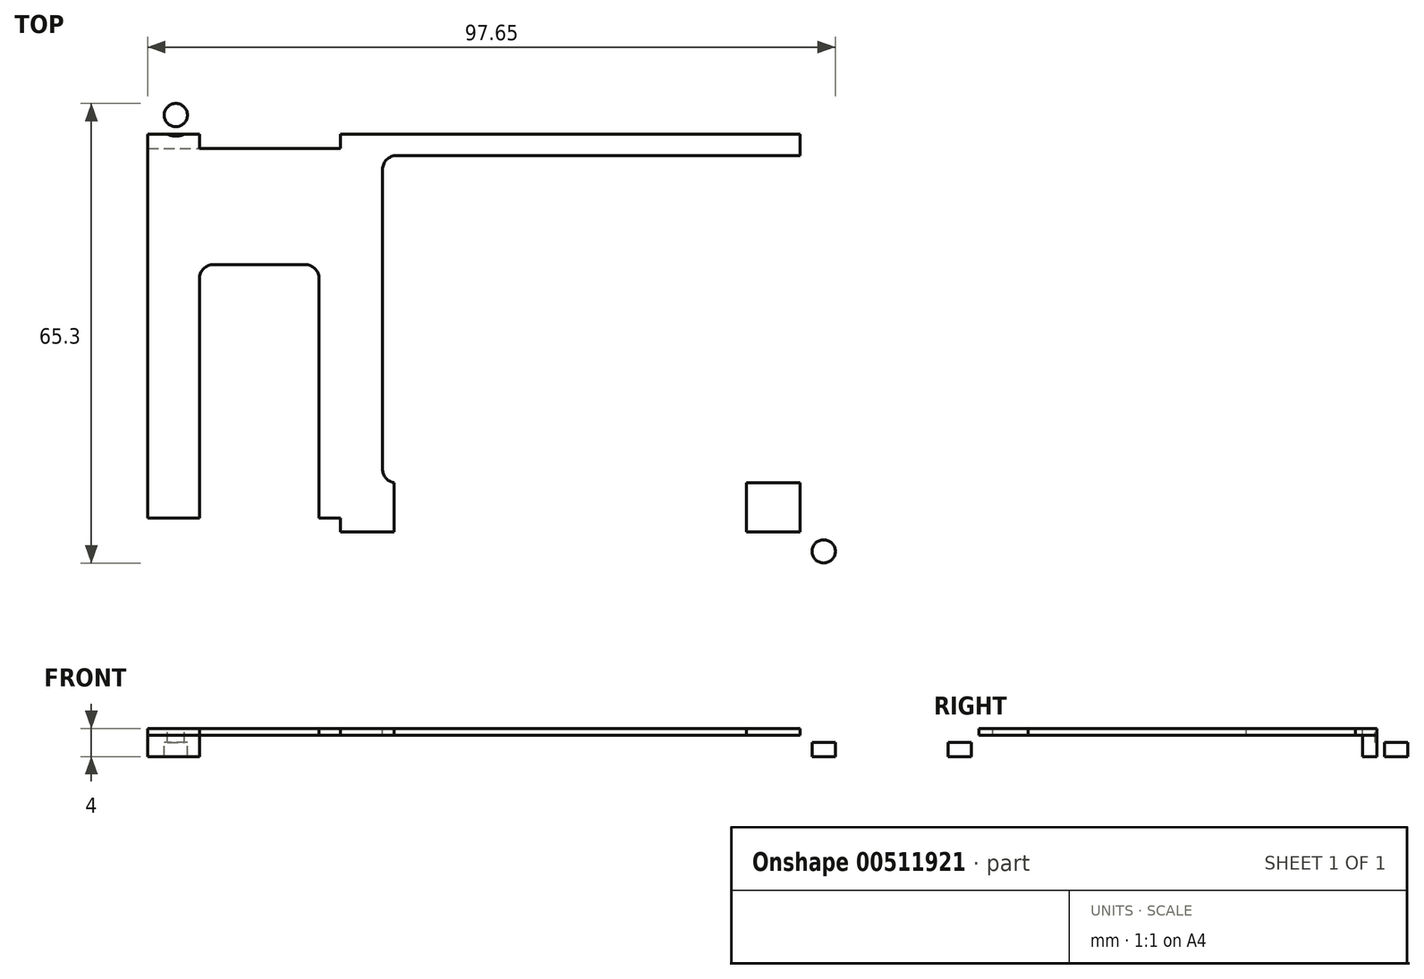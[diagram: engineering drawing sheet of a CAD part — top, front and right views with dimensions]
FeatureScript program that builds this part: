
annotation { "Feature Type Name" : "Feature", "Feature Type Description" : "" }
export const myFeature = defineFeature(function(context is Context, id is Id, definition is map)
    precondition{}
    {
        {
            var Q0;
            Q0=qCreatedBy(makeId("Top.planeOp"),FACE);
            var sketch = newSketch(context, id + "F0", { "sketchPlane" : qUnion([Q0])});
            skLineSegment(sketch, "E0.bottom", {"start": v(-50, 35) * mm, "end": v(50, 35) * mm});
            skLineSegment(sketch, "E0.top", {"start": v(-50, -35) * mm, "end": v(50, -35) * mm});
            skLineSegment(sketch, "E0.left", {"start": v(-50, 35) * mm, "end": v(-50, -35) * mm});
            skLineSegment(sketch, "E0.right", {"start": v(50, 35) * mm, "end": v(50, -35) * mm});
            skPoint(sketch, "E1", {"position": v(-50, 0) * mm});
            skPoint(sketch, "E2", {"position": v(0, 35) * mm});
            skSolve(sketch);
        }
        {
            var Q0;
            Q0=makeQuery(id+"F0.imprint","IMPRINT",FACE,{"disambiguationData":[TD([[makeQuery(id+"F0.imprint","IMPRINT",EDGE,{"derivedFrom":sQuery(id+"F0.wireOp",EDGE,"E0.bottom")}),-1.0]])]});
            extrude(context, id + "F1", {"entities" : qUnion([Q0]), "depth" : 4 * mm});
        }
        {
            var Q0;
            Q0=makeQuery(id+"F1.opExtrude","CAP_FACE",FACE,{"disambiguationData":[OSD([sQuery(id+"F0.wireOp",EDGE,"E0.bottom"),sQuery(id+"F0.wireOp",EDGE,"E0.top"),sQuery(id+"F0.wireOp",EDGE,"E0.left"),sQuery(id+"F0.wireOp",EDGE,"E0.right")])],"isStart":false});
            var sketch = newSketch(context, id + "F2", { "sketchPlane" : qUnion([Q0])});
            skLineSegment(sketch, "E3.bottom", {"start": v(-42.65, 28.25) * mm, "end": v(42.65, 28.25) * mm, "construction": true});
            skLineSegment(sketch, "E3.top", {"start": v(-42.65, -28.25) * mm, "end": v(42.65, -28.25) * mm, "construction": true});
            skLineSegment(sketch, "E3.left", {"start": v(-42.65, 28.25) * mm, "end": v(-42.65, -28.25) * mm});
            skLineSegment(sketch, "E3.right", {"start": v(42.65, 28.25) * mm, "end": v(42.65, -28.25) * mm, "construction": true});
            skPoint(sketch, "E4", {"position": v(0, 28.25) * mm});
            skPoint(sketch, "E5", {"position": v(42.65, 0) * mm});
            skCircle(sketch, "E6", {"center": v(46, 31) * mm, "radius": 1.65 * mm});
            skCircle(sketch, "E7.MirrorC", {"center": v(-46, 31) * mm, "radius": 1.65 * mm});
            skCircle(sketch, "E8.MirrorC", {"center": v(46, -31) * mm, "radius": 1.65 * mm});
            skCircle(sketch, "E9.MirrorC", {"center": v(-46, -31) * mm, "radius": 1.65 * mm});
            skLineSegment(sketch, "E10.bottom", {"start": v(-42.65, 28.25) * mm, "end": v(-50, 28.25) * mm});
            skLineSegment(sketch, "E10.top", {"start": v(-42.65, -26.25) * mm, "end": v(-50, -26.25) * mm});
            skLineSegment(sketch, "E10.left", {"start": v(-42.65, 28.25) * mm, "end": v(-42.65, -26.25) * mm, "construction": true});
            skLineSegment(sketch, "E10.right", {"start": v(-50, 28.25) * mm, "end": v(-50, -26.25) * mm});
            skLineSegment(sketch, "E11.bottom", {"start": v(42.65, 6.25) * mm, "end": v(46.15, 6.25) * mm, "construction": true});
            skLineSegment(sketch, "E11.top", {"start": v(42.65, -6.25) * mm, "end": v(46.15, -6.25) * mm, "construction": true});
            skLineSegment(sketch, "E11.left", {"start": v(42.65, 6.25) * mm, "end": v(42.65, -6.25) * mm});
            skLineSegment(sketch, "E11.right", {"start": v(46.15, 6.25) * mm, "end": v(46.15, -6.25) * mm, "construction": true});
            skLineSegment(sketch, "E12", {"start": v(-50, 26.25) * mm, "end": v(-22.65, 26.25) * mm});
            skLineSegment(sketch, "E13", {"start": v(-22.65, 26.25) * mm, "end": v(-22.65, 28.25) * mm});
            skLineSegment(sketch, "E14", {"start": v(-22.65, 28.25) * mm, "end": v(42.65, 28.25) * mm});
            skLineSegment(sketch, "E15", {"start": v(42.65, 25.25) * mm, "end": v(48, 25.25) * mm});
            skLineSegment(sketch, "E16", {"start": v(48, -21.25) * mm, "end": v(42.65, -21.25) * mm});
            skLineSegment(sketch, "E17", {"start": v(-22.65, -26.25) * mm, "end": v(-22.65, -28.25) * mm});
            skLineSegment(sketch, "E18", {"start": v(-22.65, -26.25) * mm, "end": v(-50, -26.25) * mm});
            skLineSegment(sketch, "E19", {"start": v(-50, -26.25) * mm, "end": v(-50, 26.25) * mm});
            skLineSegment(sketch, "E20", {"start": v(42.65, 28.25) * mm, "end": v(42.65, 25.25) * mm});
            skLineSegment(sketch, "E21", {"start": v(-22.65, -28.25) * mm, "end": v(-15, -28.25) * mm});
            skLineSegment(sketch, "E22", {"start": v(-15, -28.25) * mm, "end": v(-15, -21.25) * mm});
            skLineSegment(sketch, "E23", {"start": v(-15, -21.25) * mm, "end": v(35, -21.25) * mm});
            skLineSegment(sketch, "E24", {"start": v(35, -21.25) * mm, "end": v(35, -28.25) * mm});
            skLineSegment(sketch, "E25", {"start": v(35, -28.25) * mm, "end": v(42.65, -28.25) * mm});
            skLineSegment(sketch, "E26", {"start": v(42.65, -28.25) * mm, "end": v(42.65, -21.25) * mm});
            skLineSegment(sketch, "E27.bottom", {"start": v(48, 25.25) * mm, "end": v(-16.65, 25.25) * mm});
            skLineSegment(sketch, "E27.top", {"start": v(48, -21.25) * mm, "end": v(-16.65, -21.25) * mm});
            skLineSegment(sketch, "E27.left", {"start": v(48, 25.25) * mm, "end": v(48, -21.25) * mm});
            skLineSegment(sketch, "E27.right", {"start": v(-16.65, 25.25) * mm, "end": v(-16.65, -21.25) * mm});
            skLineSegment(sketch, "E28.bottom", {"start": v(-16.65, 25.25) * mm, "end": v(42.65, 25.25) * mm});
            skLineSegment(sketch, "E28.top", {"start": v(-16.65, 28.25) * mm, "end": v(42.65, 28.25) * mm});
            skLineSegment(sketch, "E28.left", {"start": v(-16.65, 25.25) * mm, "end": v(-16.65, 28.25) * mm});
            skLineSegment(sketch, "E28.right", {"start": v(42.65, 25.25) * mm, "end": v(42.65, 28.25) * mm});
            skLineSegment(sketch, "E29", {"start": v(48, -21.25) * mm, "end": v(48, -21.25) * mm});
            skLineSegment(sketch, "E30.bottom", {"start": v(-42.65, 9.75) * mm, "end": v(-25.65, 9.75) * mm});
            skLineSegment(sketch, "E30.top", {"start": v(-42.65, -26.25) * mm, "end": v(-25.65, -26.25) * mm});
            skLineSegment(sketch, "E30.left", {"start": v(-42.65, 9.75) * mm, "end": v(-42.65, -26.25) * mm});
            skLineSegment(sketch, "E30.right", {"start": v(-25.65, 9.75) * mm, "end": v(-25.65, -26.25) * mm});
            skSolve(sketch);
        }
        {
            var Q0;
            Q0=makeQuery(id+"F2.imprint","IMPRINT",FACE,{"disambiguationData":[TD([[makeQuery(id+"F2.imprint","IMPRINT",EDGE,{"derivedFrom":sQuery(id+"F2.wireOp",EDGE,"E7.MirrorC")}),-1.0]])]});
            var Q1;
            Q1=makeQuery(id+"F2.imprint","IMPRINT",FACE,{"disambiguationData":[TD([[makeQuery(id+"F2.imprint","IMPRINT",EDGE,{"derivedFrom":sQuery(id+"F2.wireOp",EDGE,"E6")}),1.0]])]});
            var Q2;
            Q2=makeQuery(id+"F2.imprint","IMPRINT",FACE,{"disambiguationData":[TD([[makeQuery(id+"F2.imprint","IMPRINT",EDGE,{"derivedFrom":sQuery(id+"F2.wireOp",EDGE,"E8.MirrorC")}),-1.0]])]});
            var Q3;
            Q3=makeQuery(id+"F2.imprint","IMPRINT",FACE,{"disambiguationData":[TD([[makeQuery(id+"F2.imprint","IMPRINT",EDGE,{"derivedFrom":sQuery(id+"F2.wireOp",EDGE,"E9.MirrorC")}),1.0]])]});
            extrude(context, id + "F3", {"entities" : qUnion([Q0, Q1, Q2, Q3]), "operationType" : NewBodyOperationType.REMOVE, "endBound" : BoundingType.UP_TO_NEXT, "oppositeDirection" : true, "depth" : 25 * mm});
        }
        {
            var Q0;
            Q0=makeQuery(id+"F2.imprint","IMPRINT",FACE,{"disambiguationData":[TD([[makeQuery(id+"F2.imprint","IMPRINT",EDGE,{"derivedFrom":sQuery(id+"F2.wireOp",EDGE,"E27.bottom")}),1.0]])]});
            var Q1;
            Q1=makeQuery(id+"F2.imprint","IMPRINT",FACE,{"disambiguationData":[TD([[makeQuery(id+"F2.imprint","IMPRINT",EDGE,{"derivedFrom":sQuery(id+"F2.wireOp",EDGE,"E28.bottom")}),1.0]])]});
            var Q2;
            {var subQ5=sQuery(id+"F2.wireOp",EDGE,"E19");Q2=makeQuery(id+"F2.imprint","IMPRINT",FACE,{"disambiguationData":[TD([[makeQuery(id+"F2.imprint","IMPRINT",EDGE,{"derivedFrom":subQ5}),1.0]])]});}
            var Q3;
            Q3=makeQuery(id+"F2.imprint","IMPRINT",FACE,{"disambiguationData":[TD([[makeQuery(id+"F2.imprint","IMPRINT",EDGE,{"derivedFrom":sQuery(id+"F2.wireOp",EDGE,"E30.bottom")}),-1.0]])]});
            extrude(context, id + "F4", {"entities" : qUnion([Q0, Q1, Q2, Q3]), "operationType" : NewBodyOperationType.REMOVE, "endBound" : BoundingType.UP_TO_NEXT, "oppositeDirection" : true, "depth" : 25 * mm});
        }
        {
            var Q0;
            Q0=makeQuery(id+"F0.imprint","IMPRINT",FACE,{"disambiguationData":[TD([[makeQuery(id+"F0.imprint","IMPRINT",EDGE,{"derivedFrom":sQuery(id+"F0.wireOp",EDGE,"E0.bottom")}),-1.0]])]});
            var sketch = newSketch(context, id + "F5", { "sketchPlane" : qUnion([Q0])});
            skLineSegment(sketch, "E31.0", {"start": v(-22.65, -26.25) * mm, "end": v(-50, -26.25) * mm});
            skLineSegment(sketch, "E32.0", {"start": v(-50, 26.25) * mm, "end": v(-22.65, 26.25) * mm});
            skPoint(sketch, "E33.0", {"position": v(-22.65, 27.25) * mm});
            skLineSegment(sketch, "E34.0", {"start": v(-22.65, 26.25) * mm, "end": v(-22.65, 28.25) * mm});
            skLineSegment(sketch, "E35.0", {"start": v(-22.65, 28.25) * mm, "end": v(42.65, 28.25) * mm});
            skLineSegment(sketch, "E36.0", {"start": v(-22.65, -26.25) * mm, "end": v(-22.65, -28.25) * mm});
            skLineSegment(sketch, "E37.0", {"start": v(-22.65, -28.25) * mm, "end": v(-15, -28.25) * mm});
            skLineSegment(sketch, "E38.0", {"start": v(-15, -28.25) * mm, "end": v(-15, -21.25) * mm});
            skLineSegment(sketch, "E39.0", {"start": v(35, -21.25) * mm, "end": v(35, -28.25) * mm});
            skLineSegment(sketch, "E40.0", {"start": v(42.65, -28.25) * mm, "end": v(42.65, -21.25) * mm});
            skLineSegment(sketch, "E41.0", {"start": v(48, -21.25) * mm, "end": v(42.65, -21.25) * mm});
            skLineSegment(sketch, "E42", {"start": v(35, -28.25) * mm, "end": v(42.65, -28.25) * mm});
            skLineSegment(sketch, "E43", {"start": v(-50, -26.25) * mm, "end": v(-50, 26.25) * mm});
            skLineSegment(sketch, "E44.0", {"start": v(42.65, 28.25) * mm, "end": v(42.65, 25.25) * mm});
            skLineSegment(sketch, "E45.0", {"start": v(42.65, 25.25) * mm, "end": v(48, 25.25) * mm});
            skLineSegment(sketch, "E46", {"start": v(48, -21.25) * mm, "end": v(48, 25.25) * mm});
            skLineSegment(sketch, "E47", {"start": v(-15, -21.25) * mm, "end": v(35, -21.25) * mm});
            skSolve(sketch);
        }
        {
            var Q0;
            Q0=makeQuery(id+"F5.imprint","IMPRINT",FACE,{"disambiguationData":[TD([[makeQuery(id+"F5.imprint","IMPRINT",EDGE,{"derivedFrom":sQuery(id+"F5.wireOp",EDGE,"E31.0")}),-1.0]])]});
            extrude(context, id + "F6", {"entities" : qUnion([Q0]), "operationType" : NewBodyOperationType.REMOVE, "depth" : 3 * mm});
        }
        {
            var Q0;
            Q0=makeQuery(id+"F1.opExtrude","CAP_FACE",FACE,{"disambiguationData":[OSD([sQuery(id+"F0.wireOp",EDGE,"E0.bottom"),sQuery(id+"F0.wireOp",EDGE,"E0.top"),sQuery(id+"F0.wireOp",EDGE,"E0.left"),sQuery(id+"F0.wireOp",EDGE,"E0.right")])],"isStart":false});
            var sketch = newSketch(context, id + "F7", { "sketchPlane" : qUnion([Q0])});
            skCircle(sketch, "E48", {"center": v(-46, 31) * mm, "radius": 3 * mm});
            skCircle(sketch, "E49", {"center": v(46, 31) * mm, "radius": 3 * mm});
            skCircle(sketch, "E50", {"center": v(46, -31) * mm, "radius": 3 * mm});
            skCircle(sketch, "E51", {"center": v(-46, -31) * mm, "radius": 3 * mm});
            skSolve(sketch);
        }
        {
            var Q0;
            Q0 = qSketchRegion(id + "F7", true);
            extrude(context, id + "F8", {"entities" : qUnion([Q0]), "operationType" : NewBodyOperationType.REMOVE, "oppositeDirection" : true, "depth" : 2 * mm});
        }
        {
            var Q0;
            Q0=makeQuery(id+"F1.opExtrude","SWEPT_EDGE",EDGE,{"disambiguationData":[OSD([sQuery(id+"F0.wireOp",EDGE,"E0.bottom"),sQuery(id+"F0.wireOp",EDGE,"E0.left")])]});
            var Q1;
            Q1=makeQuery(id+"F1.opExtrude","SWEPT_EDGE",EDGE,{"disambiguationData":[OSD([sQuery(id+"F0.wireOp",EDGE,"E0.top"),sQuery(id+"F0.wireOp",EDGE,"E0.left")])]});
            var Q2;
            Q2=makeQuery(id+"F1.opExtrude","SWEPT_EDGE",EDGE,{"disambiguationData":[OSD([sQuery(id+"F0.wireOp",EDGE,"E0.top"),sQuery(id+"F0.wireOp",EDGE,"E0.right")])]});
            var Q3;
            Q3=makeQuery(id+"F1.opExtrude","SWEPT_EDGE",EDGE,{"disambiguationData":[OSD([sQuery(id+"F0.wireOp",EDGE,"E0.bottom"),sQuery(id+"F0.wireOp",EDGE,"E0.right")])]});
            var Q4;
            Q4=makeQuery(id+"F4.boolean.opBoolean","COPY",EDGE,{"derivedFrom":makeQuery(id+"F4.opExtrude","SWEPT_EDGE",EDGE,{"disambiguationData":[OSD([sQuery(id+"F2.wireOp",EDGE,"E27.top"),sQuery(id+"F2.wireOp",EDGE,"E27.right")])]})});
            var Q5;
            Q5=makeQuery(id+"F4.boolean.opBoolean","COPY",EDGE,{"derivedFrom":makeQuery(id+"F4.opExtrude","SWEPT_EDGE",EDGE,{"disambiguationData":[OSD([sQuery(id+"F2.wireOp",EDGE,"E14"),sQuery(id+"F2.wireOp",EDGE,"E28.top"),sQuery(id+"F2.wireOp",EDGE,"E28.left")])]})});
            var Q6;
            Q6=makeQuery(id+"F4.boolean.opBoolean","COPY",EDGE,{"derivedFrom":makeQuery(id+"F4.opExtrude","SWEPT_EDGE",EDGE,{"disambiguationData":[OSD([sQuery(id+"F2.wireOp",EDGE,"E10.right"),sQuery(id+"F2.wireOp",EDGE,"E12"),sQuery(id+"F2.wireOp",EDGE,"E19")])]})});
            var Q7;
            Q7=makeQuery(id+"F4.boolean.opBoolean","COPY",EDGE,{"derivedFrom":makeQuery(id+"F4.opExtrude","SWEPT_EDGE",EDGE,{"disambiguationData":[OSD([sQuery(id+"F0.wireOp",EDGE,"E0.left"),sQuery(id+"F2.wireOp",EDGE,"E18"),sQuery(id+"F2.wireOp",EDGE,"E19")])]})});
            var Q8;
            Q8=makeQuery(id+"F4.boolean.opBoolean","COPY",EDGE,{"derivedFrom":makeQuery(id+"F4.opExtrude","SWEPT_EDGE",EDGE,{"disambiguationData":[OSD([sQuery(id+"F2.wireOp",EDGE,"E3.left"),sQuery(id+"F2.wireOp",EDGE,"E12")])]})});
            var Q9;
            Q9=makeQuery(id+"F4.boolean.opBoolean","COPY",EDGE,{"derivedFrom":makeQuery(id+"F4.opExtrude","SWEPT_EDGE",EDGE,{"disambiguationData":[OSD([sQuery(id+"F2.wireOp",EDGE,"E3.left"),sQuery(id+"F2.wireOp",EDGE,"E18")])]})});
            var Q10;
            Q10=makeQuery(id+"F4.boolean.opBoolean","COPY",EDGE,{"derivedFrom":makeQuery(id+"F4.opExtrude","SWEPT_EDGE",EDGE,{"disambiguationData":[OSD([sQuery(id+"F2.wireOp",EDGE,"E3.left"),sQuery(id+"F2.wireOp",EDGE,"E30.bottom"),sQuery(id+"F2.wireOp",EDGE,"E30.left")])]})});
            var Q11;
            Q11=makeQuery(id+"F4.boolean.opBoolean","COPY",EDGE,{"derivedFrom":makeQuery(id+"F4.opExtrude","SWEPT_EDGE",EDGE,{"disambiguationData":[OSD([sQuery(id+"F2.wireOp",EDGE,"E30.bottom"),sQuery(id+"F2.wireOp",EDGE,"E30.right")])]})});
            var Q12;
            Q12=makeQuery(id+"F4.boolean.opBoolean","COPY",EDGE,{"derivedFrom":makeQuery(id+"F4.opExtrude","SWEPT_EDGE",EDGE,{"disambiguationData":[OSD([sQuery(id+"F2.wireOp",EDGE,"E18"),sQuery(id+"F2.wireOp",EDGE,"E30.top"),sQuery(id+"F2.wireOp",EDGE,"E30.right")])]})});
            fillet(context, id + "F9", {"entities" : qUnion([Q0, Q1, Q2, Q3, Q4, Q5, Q6, Q7, Q8, Q9, Q10, Q11, Q12]), "radius" : 2 * mm, "tangentPropagation" : true, "allowEdgeOverflow" : false});
        }
    });
